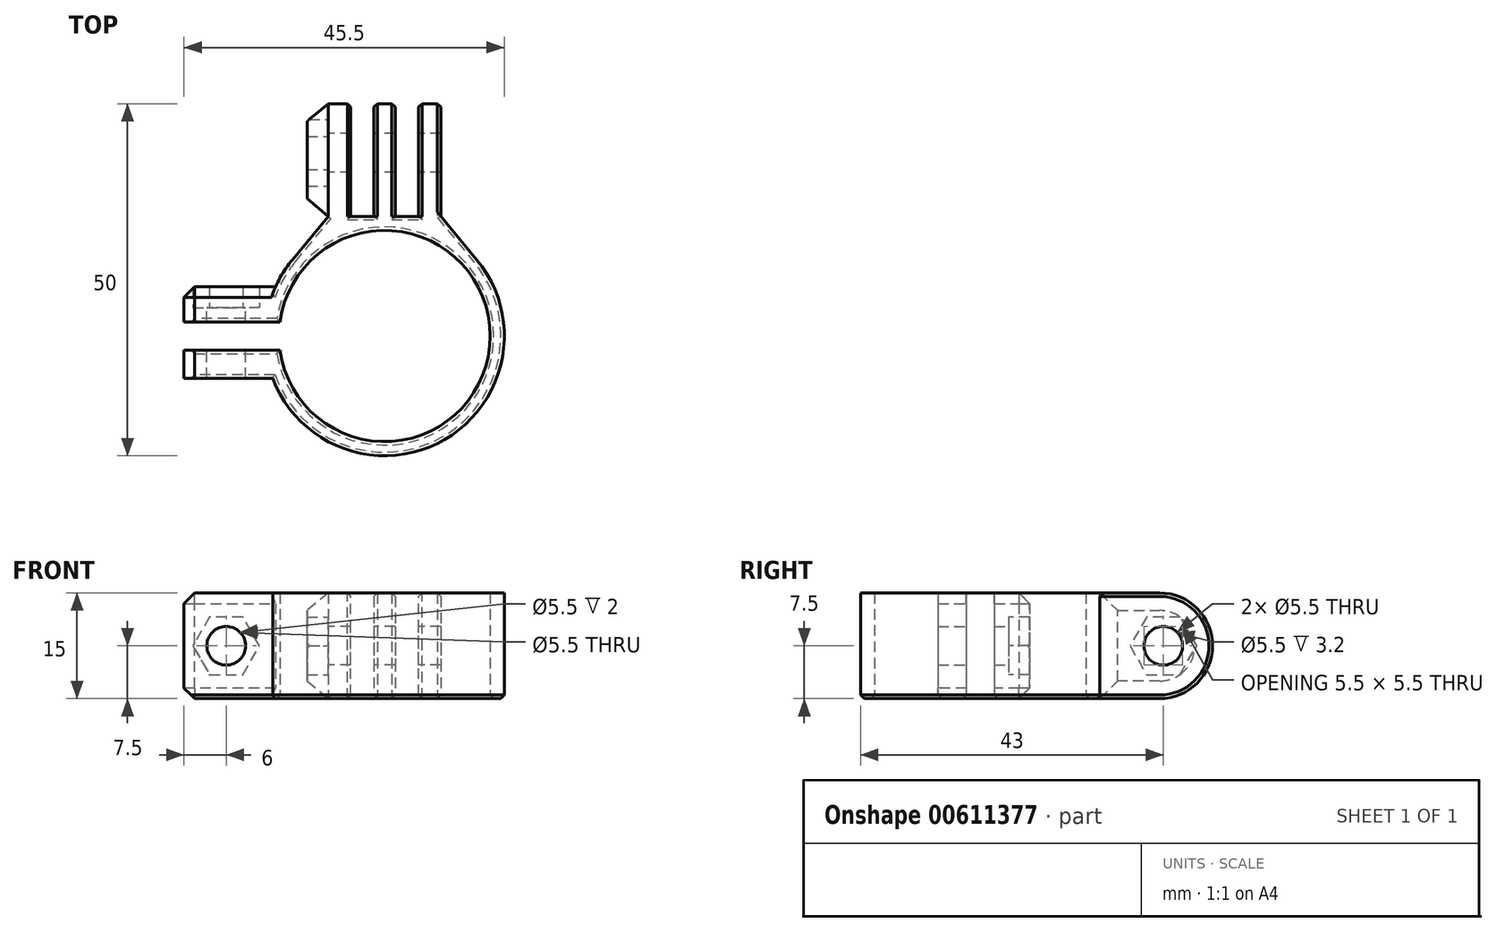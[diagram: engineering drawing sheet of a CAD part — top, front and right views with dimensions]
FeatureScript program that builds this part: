
annotation { "Feature Type Name" : "Feature", "Feature Type Description" : "" }
export const myFeature = defineFeature(function(context is Context, id is Id, definition is map)
    precondition{}
    {
        {
            var Q0;
            Q0=qCreatedBy(makeId("Top.planeOp"),FACE);
            var sketch = newSketch(context, id + "F0", { "sketchPlane" : qUnion([Q0])});
            skCircle(sketch, "E0", {"center": v(0, 0) * mm, "radius": 15 * mm});
            skCircle(sketch, "E1", {"center": v(0, 0) * mm, "radius": 17 * mm});
            skLineSegment(sketch, "E2", {"start": v(0, 17) * mm, "end": v(8, 17) * mm});
            skLineSegment(sketch, "E3", {"start": v(0, 17) * mm, "end": v(-8, 17) * mm});
            skLineSegment(sketch, "E4", {"start": v(-8, 17) * mm, "end": v(-13.1, 10.84) * mm});
            skLineSegment(sketch, "E5", {"start": v(8, 17) * mm, "end": v(13.1, 10.84) * mm});
            skLineSegment(sketch, "E6", {"start": v(13.1, 10.84) * mm, "end": v(11.56, 9.56) * mm});
            skLineSegment(sketch, "E7", {"start": v(-13.1, 10.84) * mm, "end": v(-11.56, 9.56) * mm});
            skLineSegment(sketch, "E8.bottom", {"start": v(-28.5, 2) * mm, "end": v(-10, 2) * mm});
            skLineSegment(sketch, "E8.top", {"start": v(-28.5, -2) * mm, "end": v(-10, -2) * mm});
            skLineSegment(sketch, "E8.left", {"start": v(-28.5, 2) * mm, "end": v(-28.5, -2) * mm});
            skLineSegment(sketch, "E8.right", {"start": v(-10, 2) * mm, "end": v(-10, -2) * mm});
            skLineSegment(sketch, "E9.bottom", {"start": v(-28.5, 2) * mm, "end": v(-16.52, 2) * mm});
            skLineSegment(sketch, "E9.top", {"start": v(-28.5, 4) * mm, "end": v(-16.52, 4) * mm});
            skLineSegment(sketch, "E9.left", {"start": v(-28.5, 2) * mm, "end": v(-28.5, 4) * mm});
            skLineSegment(sketch, "E9.right", {"start": v(-16.52, 2) * mm, "end": v(-16.52, 4) * mm});
            skLineSegment(sketch, "E10.bottom", {"start": v(-28.5, -2) * mm, "end": v(-16.52, -2) * mm});
            skLineSegment(sketch, "E10.top", {"start": v(-28.5, -4) * mm, "end": v(-16.52, -4) * mm});
            skLineSegment(sketch, "E10.left", {"start": v(-28.5, -2) * mm, "end": v(-28.5, -4) * mm});
            skLineSegment(sketch, "E10.right", {"start": v(-16.52, -2) * mm, "end": v(-16.52, -4) * mm});
            skSolve(sketch);
        }
        {
            var Q0;
            {var subQ0=sQuery(id+"F0.wireOp",EDGE,"E9.top");Q0=makeQuery(id+"F0.imprint","IMPRINT",FACE,{"disambiguationData":[TD([[makeQuery(id+"F0.imprint","IMPRINT",EDGE,{"derivedFrom":subQ0}),-1.0]])]});}
            var Q1;
            {var subQ0=sQuery(id+"F0.wireOp",EDGE,"E9.right");Q1=makeQuery(id+"F0.imprint","IMPRINT",FACE,{"disambiguationData":[TD([[makeQuery(id+"F0.imprint","IMPRINT",EDGE,{"derivedFrom":subQ0}),1.0]])]});}
            var Q2;
            {var subQ4=sQuery(id+"F0.wireOp",EDGE,"E7");Q2=makeQuery(id+"F0.imprint","IMPRINT",FACE,{"disambiguationData":[TD([[makeQuery(id+"F0.imprint","IMPRINT",EDGE,{"derivedFrom":subQ4}),-1.0]])]});}
            var Q3;
            {var subQ2=sQuery(id+"F0.wireOp",EDGE,"E6");Q3=makeQuery(id+"F0.imprint","IMPRINT",FACE,{"disambiguationData":[TD([[makeQuery(id+"F0.imprint","IMPRINT",EDGE,{"derivedFrom":subQ2}),-1.0]])]});}
            var Q4;
            {var subQ0=sQuery(id+"F0.wireOp",EDGE,"E3");Q4=makeQuery(id+"F0.imprint","IMPRINT",FACE,{"disambiguationData":[TD([[makeQuery(id+"F0.imprint","IMPRINT",EDGE,{"derivedFrom":subQ0}),1.0]])]});}
            var Q5;
            {var subQ0=sQuery(id+"F0.wireOp",EDGE,"E2");Q5=makeQuery(id+"F0.imprint","IMPRINT",FACE,{"disambiguationData":[TD([[makeQuery(id+"F0.imprint","IMPRINT",EDGE,{"derivedFrom":subQ0}),-1.0]])]});}
            var Q6;
            {var subQ4=sQuery(id+"F0.wireOp",EDGE,"E6");Q6=makeQuery(id+"F0.imprint","IMPRINT",FACE,{"disambiguationData":[TD([[makeQuery(id+"F0.imprint","IMPRINT",EDGE,{"derivedFrom":subQ4}),1.0]])]});}
            var Q7;
            {var subQ0=sQuery(id+"F0.wireOp",EDGE,"E10.right");Q7=makeQuery(id+"F0.imprint","IMPRINT",FACE,{"disambiguationData":[TD([[makeQuery(id+"F0.imprint","IMPRINT",EDGE,{"derivedFrom":subQ0}),-1.0]])]});}
            var Q8;
            {var subQ0=sQuery(id+"F0.wireOp",EDGE,"E10.top");Q8=makeQuery(id+"F0.imprint","IMPRINT",FACE,{"disambiguationData":[TD([[makeQuery(id+"F0.imprint","IMPRINT",EDGE,{"derivedFrom":subQ0}),1.0]])]});}
            extrude(context, id + "F1", {"entities" : qUnion([Q0, Q1, Q2, Q3, Q4, Q5, Q6, Q7, Q8]), "depth" : 15 * mm, "offsetDistance" : 25 * mm});
        }
        {
            var Q0;
            Q0=makeQuery(id+"F1.opExtrude","SWEPT_FACE",FACE,{"disambiguationData":[OSD([sQuery(id+"F0.wireOp",EDGE,"E9.top")])]});
            var sketch = newSketch(context, id + "F2", { "sketchPlane" : qUnion([Q0])});
            skCircle(sketch, "E11", {"center": v(22.5, 7.5) * mm, "radius": 2.75 * mm});
            skCircle(sketch, "E12.cCircle", {"center": v(22.5, 7.5) * mm, "radius": 4.1 * mm, "construction": true});
            skLineSegment(sketch, "E12.0", {"start": v(27.23, 7.5) * mm, "end": v(24.87, 3.4) * mm});
            skLineSegment(sketch, "E12.1", {"start": v(24.87, 3.4) * mm, "end": v(20.13, 3.4) * mm});
            skLineSegment(sketch, "E12.2", {"start": v(20.13, 3.4) * mm, "end": v(17.77, 7.5) * mm});
            skLineSegment(sketch, "E12.3", {"start": v(17.77, 7.5) * mm, "end": v(20.13, 11.6) * mm});
            skLineSegment(sketch, "E12.4", {"start": v(20.13, 11.6) * mm, "end": v(24.87, 11.6) * mm});
            skLineSegment(sketch, "E12.5", {"start": v(24.87, 11.6) * mm, "end": v(27.23, 7.5) * mm});
            skPoint(sketch, "E12.0.midPoint", {"position": v(26.05, 5.45) * mm});
            skLineSegment(sketch, "E13.0", {"start": v(16.03, 7.5) * mm, "end": v(19.27, 13.1) * mm});
            skLineSegment(sketch, "E13.1", {"start": v(25.73, 13.1) * mm, "end": v(28.97, 7.5) * mm});
            skLineSegment(sketch, "E13.2", {"start": v(28.97, 7.5) * mm, "end": v(25.73, 1.9) * mm});
            skLineSegment(sketch, "E13.3", {"start": v(19.27, 13.1) * mm, "end": v(25.73, 13.1) * mm});
            skLineSegment(sketch, "E13.4", {"start": v(25.73, 1.9) * mm, "end": v(19.27, 1.9) * mm});
            skLineSegment(sketch, "E13.5", {"start": v(19.27, 1.9) * mm, "end": v(16.03, 7.5) * mm});
            skSolve(sketch);
        }
        {
            var Q0;
            Q0=makeQuery(id+"F2.imprint","IMPRINT",FACE,{"disambiguationData":[TD([[makeQuery(id+"F2.imprint","IMPRINT",EDGE,{"derivedFrom":sQuery(id+"F2.wireOp",EDGE,"E11")}),1.0]])]});
            extrude(context, id + "F3", {"entities" : qUnion([Q0]), "operationType" : NewBodyOperationType.REMOVE, "endBound" : BoundingType.THROUGH_ALL, "oppositeDirection" : true, "depth" : 25 * mm, "offsetDistance" : 25 * mm});
        }
        {
            var Q0;
            Q0=makeQuery(id+"F2.imprint","IMPRINT",FACE,{"disambiguationData":[TD([[makeQuery(id+"F2.imprint","IMPRINT",EDGE,{"derivedFrom":sQuery(id+"F2.wireOp",EDGE,"E13.0")}),1.0]])]});
            var Q1;
            Q1=makeQuery(id+"F2.imprint","IMPRINT",FACE,{"disambiguationData":[TD([[makeQuery(id+"F2.imprint","IMPRINT",EDGE,{"derivedFrom":sQuery(id+"F2.wireOp",EDGE,"E12.0")}),1.0]])]});
            var Q2;
            {var subQ1=sQuery(id+"F2.wireOp",EDGE,"E13.4");Q2=makeQuery(id+"F2.imprint","IMPRINT",FACE,{"disambiguationData":[TD([[makeQuery(id+"F2.imprint","IMPRINT",EDGE,{"derivedFrom":subQ1}),1.0]])]});}
            extrude(context, id + "F4", {"entities" : qUnion([Q0, Q1, Q2]), "operationType" : NewBodyOperationType.ADD, "depth" : 3 * mm, "offsetDistance" : 25 * mm});
        }
        {
            var Q0;
            Q0=makeQuery(id+"F4.opExtrude","SWEPT_FACE",FACE,{"disambiguationData":[OSD([sQuery(id+"F0.wireOp",EDGE,"E1"),sQuery(id+"F0.wireOp",EDGE,"E9.top"),sQuery(id+"F0.wireOp",EDGE,"E9.right")])]});
            extrude(context, id + "F5", {"entities" : qUnion([Q0]), "operationType" : NewBodyOperationType.ADD, "endBound" : BoundingType.UP_TO_NEXT, "depth" : 25 * mm, "offsetDistance" : 25 * mm});
        }
        {
            var Q0;
            Q0=makeQuery(id+"F1.opExtrude","SWEPT_FACE",FACE,{"disambiguationData":[OSD([sQuery(id+"F0.wireOp",EDGE,"E2"),sQuery(id+"F0.wireOp",EDGE,"E3")])]});
            var sketch = newSketch(context, id + "F6", { "sketchPlane" : qUnion([Q0])});
            skLineSegment(sketch, "E14.bottom", {"start": v(-8, 0) * mm, "end": v(-4.8, 0) * mm});
            skLineSegment(sketch, "E14.top", {"start": v(-8, 15) * mm, "end": v(-4.8, 15) * mm});
            skLineSegment(sketch, "E14.left", {"start": v(-8, 0) * mm, "end": v(-8, 15) * mm});
            skLineSegment(sketch, "E14.right", {"start": v(-4.8, 0) * mm, "end": v(-4.8, 15) * mm});
            skLineSegment(sketch, "E15.bottom", {"start": v(8, 0) * mm, "end": v(4.8, 0) * mm});
            skLineSegment(sketch, "E15.top", {"start": v(8, 15) * mm, "end": v(4.8, 15) * mm});
            skLineSegment(sketch, "E15.left", {"start": v(8, 0) * mm, "end": v(8, 15) * mm});
            skLineSegment(sketch, "E15.right", {"start": v(4.8, 0) * mm, "end": v(4.8, 15) * mm});
            skLineSegment(sketch, "E16.bottom", {"start": v(-1.5, 15) * mm, "end": v(1.5, 15) * mm});
            skLineSegment(sketch, "E16.top", {"start": v(-1.5, 0) * mm, "end": v(1.5, 0) * mm});
            skLineSegment(sketch, "E16.left", {"start": v(-1.5, 15) * mm, "end": v(-1.5, 0) * mm});
            skLineSegment(sketch, "E16.right", {"start": v(1.5, 15) * mm, "end": v(1.5, 0) * mm});
            skSolve(sketch);
        }
        {
            var Q0;
            Q0=makeQuery(id+"F6.imprint","IMPRINT",FACE,{"disambiguationData":[TD([[makeQuery(id+"F6.imprint","IMPRINT",EDGE,{"derivedFrom":sQuery(id+"F6.wireOp",EDGE,"E14.bottom")}),1.0]])]});
            var Q1;
            Q1=makeQuery(id+"F6.imprint","IMPRINT",FACE,{"disambiguationData":[TD([[makeQuery(id+"F6.imprint","IMPRINT",EDGE,{"derivedFrom":sQuery(id+"F6.wireOp",EDGE,"E16.bottom")}),-1.0]])]});
            var Q2;
            Q2=makeQuery(id+"F6.imprint","IMPRINT",FACE,{"disambiguationData":[TD([[makeQuery(id+"F6.imprint","IMPRINT",EDGE,{"derivedFrom":sQuery(id+"F6.wireOp",EDGE,"E15.bottom")}),1.0]])]});
            extrude(context, id + "F7", {"entities" : qUnion([Q0, Q1, Q2]), "operationType" : NewBodyOperationType.ADD, "depth" : 16 * mm, "offsetDistance" : 25 * mm});
        }
        {
            var Q0;
            Q0=makeQuery(id+"F7.opExtrude","SWEPT_FACE",FACE,{"disambiguationData":[OSD([sQuery(id+"F6.wireOp",EDGE,"E15.left")])]});
            var sketch = newSketch(context, id + "F8", { "sketchPlane" : qUnion([Q0])});
            skCircle(sketch, "E17", {"center": v(-26, 7.5) * mm, "radius": 2.75 * mm});
            skPoint(sketch, "E18.0.midPoint", {"position": v(-30.1, 7.5) * mm});
            skCircle(sketch, "E19.cCircle", {"center": v(-26, 7.5) * mm, "radius": 4.1 * mm, "construction": true});
            skLineSegment(sketch, "E19.0", {"start": v(-28.37, 11.6) * mm, "end": v(-23.63, 11.6) * mm});
            skLineSegment(sketch, "E19.1", {"start": v(-23.63, 11.6) * mm, "end": v(-21.27, 7.5) * mm});
            skLineSegment(sketch, "E19.2", {"start": v(-21.27, 7.5) * mm, "end": v(-23.63, 3.4) * mm});
            skLineSegment(sketch, "E19.3", {"start": v(-23.63, 3.4) * mm, "end": v(-28.37, 3.4) * mm});
            skLineSegment(sketch, "E19.4", {"start": v(-28.37, 3.4) * mm, "end": v(-30.73, 7.5) * mm});
            skLineSegment(sketch, "E19.5", {"start": v(-30.73, 7.5) * mm, "end": v(-28.37, 11.6) * mm});
            skPoint(sketch, "E19.0.midPoint", {"position": v(-26, 11.6) * mm});
            skLineSegment(sketch, "E20.0", {"start": v(-22.77, 13.1) * mm, "end": v(-19.53, 7.5) * mm});
            skLineSegment(sketch, "E20.1", {"start": v(-22.77, 1.9) * mm, "end": v(-29.23, 1.9) * mm});
            skLineSegment(sketch, "E20.2", {"start": v(-29.23, 1.9) * mm, "end": v(-32.47, 7.5) * mm});
            skLineSegment(sketch, "E20.3", {"start": v(-19.53, 7.5) * mm, "end": v(-22.77, 1.9) * mm});
            skLineSegment(sketch, "E20.4", {"start": v(-32.47, 7.5) * mm, "end": v(-29.23, 13.1) * mm});
            skLineSegment(sketch, "E20.5", {"start": v(-29.23, 13.1) * mm, "end": v(-22.77, 13.1) * mm});
            skSolve(sketch);
        }
        {
            var Q0;
            Q0=makeQuery(id+"F8.imprint","IMPRINT",FACE,{"disambiguationData":[TD([[makeQuery(id+"F8.imprint","IMPRINT",EDGE,{"derivedFrom":sQuery(id+"F8.wireOp",EDGE,"E17")}),1.0]])]});
            extrude(context, id + "F9", {"entities" : qUnion([Q0]), "operationType" : NewBodyOperationType.REMOVE, "endBound" : BoundingType.THROUGH_ALL, "oppositeDirection" : true, "depth" : 25 * mm, "offsetDistance" : 25 * mm});
        }
        {
            var Q0;
            Q0=makeQuery(id+"F8.imprint","IMPRINT",FACE,{"disambiguationData":[TD([[makeQuery(id+"F8.imprint","IMPRINT",EDGE,{"derivedFrom":sQuery(id+"F8.wireOp",EDGE,"E19.0")}),1.0]])]});
            extrude(context, id + "F10", {"entities" : qUnion([Q0]), "operationType" : NewBodyOperationType.ADD, "depth" : 3 * mm, "offsetDistance" : 25 * mm});
        }
        {
            var Q0;
            Q0=makeQuery(id+"F7.opExtrude","CAP_EDGE",EDGE,{"disambiguationData":[OSD([sQuery(id+"F6.wireOp",EDGE,"E14.bottom")])],"isStart":false});
            var Q1;
            Q1=makeQuery(id+"F7.opExtrude","CAP_EDGE",EDGE,{"disambiguationData":[OSD([sQuery(id+"F6.wireOp",EDGE,"E16.top")])],"isStart":false});
            var Q2;
            Q2=makeQuery(id+"F7.opExtrude","CAP_EDGE",EDGE,{"disambiguationData":[OSD([sQuery(id+"F6.wireOp",EDGE,"E15.bottom")])],"isStart":false});
            var Q3;
            Q3=makeQuery(id+"F7.opExtrude","CAP_EDGE",EDGE,{"disambiguationData":[OSD([sQuery(id+"F6.wireOp",EDGE,"E15.top")])],"isStart":false});
            var Q4;
            Q4=makeQuery(id+"F7.opExtrude","CAP_EDGE",EDGE,{"disambiguationData":[OSD([sQuery(id+"F6.wireOp",EDGE,"E16.bottom")])],"isStart":false});
            var Q5;
            Q5=makeQuery(id+"F7.opExtrude","CAP_EDGE",EDGE,{"disambiguationData":[OSD([sQuery(id+"F6.wireOp",EDGE,"E14.top")])],"isStart":false});
            fillet(context, id + "F11", {"entities" : qUnion([Q0, Q1, Q2, Q3, Q4, Q5]), "radius" : 7.5 * mm, "tangentPropagation" : true, "allowEdgeOverflow" : false});
        }
        {
            var Q0;
            {var subQ7=sQuery(id+"F0.wireOp",EDGE,"E4");var subQ19=sQuery(id+"F6.wireOp",EDGE,"E15.left");Q0=makeQuery(id+"F10.boolean.opBoolean","SPLIT",FACE,{"disambiguationData":[TD([makeQuery(id+"F1.opExtrude","SWEPT_FACE",FACE,{"disambiguationData":[OSD([subQ7])]})])],"derivedFrom":makeQuery(id+"F7.opExtrude","SWEPT_FACE",FACE,{"disambiguationData":[OSD([subQ19])]})});}
            extrude(context, id + "F12", {"entities" : qUnion([Q0]), "operationType" : NewBodyOperationType.ADD, "depth" : 3 * mm, "offsetDistance" : 25 * mm});
        }
        {
            var Q0;
            Q0=makeQuery(id+"F12.opExtrude","CAP_EDGE",EDGE,{"disambiguationData":[OSD([sQuery(id+"F0.wireOp",EDGE,"E3"),sQuery(id+"F0.wireOp",EDGE,"E4"),sQuery(id+"F6.wireOp",EDGE,"E15.left")])],"isStart":false});
            var Q1;
            {var subQ7=sQuery(id+"F0.wireOp",EDGE,"E4");var subQ19=sQuery(id+"F6.wireOp",EDGE,"E15.left");var subQ20=sQuery(id+"F6.wireOp",EDGE,"E15.top");Q1=makeQuery(id+"F12.opExtrude","CAP_EDGE",EDGE,{"disambiguationData":[OSD([subQ20,subQ19]),TDD([makeQuery(id+"F11.opFillet","BLEND_EDGE",EDGE,{"blendedFrom":[makeQuery(id+"F7.opExtrude","CAP_EDGE",EDGE,{"disambiguationData":[OSD([subQ20])],"isStart":false}),makeQuery(id+"F10.boolean.opBoolean","SPLIT",FACE,{"disambiguationData":[TD([makeQuery(id+"F1.opExtrude","SWEPT_FACE",FACE,{"disambiguationData":[OSD([subQ7])]})])],"derivedFrom":makeQuery(id+"F7.opExtrude","SWEPT_FACE",FACE,{"disambiguationData":[OSD([subQ19])]})})],"blendedInto":[makeQuery(id+"F10.boolean.opBoolean","SPLIT",FACE,{"disambiguationData":[TD([makeQuery(id+"F1.opExtrude","SWEPT_FACE",FACE,{"disambiguationData":[OSD([subQ7])]})])],"derivedFrom":makeQuery(id+"F7.opExtrude","SWEPT_FACE",FACE,{"disambiguationData":[OSD([subQ19])]})})]})])],"isStart":false});}
            chamfer(context, id + "F13", {"entities" : qUnion([Q0, Q1]), "chamferType" : ChamferType.TWO_OFFSETS, "width1" : 3 * mm, "oppositeDirection" : false, "width2" : 2.5 * mm, "tangentPropagation" : true});
        }
        {
            var Q0;
            {var subQ0=sQuery(id+"F0.wireOp",EDGE,"E9.top");var subQ1=makeQuery(id+"F1.opExtrude","CAP_EDGE",EDGE,{"disambiguationData":[OSD([subQ0])],"isStart":true});var subQ2=sQuery(id+"F0.wireOp",EDGE,"E9.right");var subQ3=sQuery(id+"F0.wireOp",EDGE,"E1");Q0=makeQuery(id+"F5.boolean.opBoolean","MERGE",EDGE,{"derivedFrom":[makeQuery(id+"F4.opExtrude","CAP_EDGE",EDGE,{"disambiguationData":[OSD([subQ0]),TDD([makeQuery(id+"F2.imprint","IMPRINT",EDGE,{"derivedFrom":subQ1})])],"isStart":false}),makeQuery(id+"F5.opExtrude","SWEPT_EDGE",EDGE,{"disambiguationData":[OSD([subQ3,subQ0,subQ2]),TDD([makeQuery(id+"F4.opExtrude","CAP_VERTEX",VERTEX,{"disambiguationData":[OSD([subQ3,subQ0,subQ2]),TDD([makeQuery(id+"F2.imprint","INTERSECT",VERTEX,{"derivedFrom":[makeQuery(id+"F1.opExtrude","SWEPT_EDGE",EDGE,{"disambiguationData":[OSD([subQ3,subQ0,subQ2])]}),subQ1]})])],"isStart":false})])]})]});}
            var Q1;
            Q1=makeQuery(id+"F4.opExtrude","CAP_EDGE",EDGE,{"disambiguationData":[OSD([sQuery(id+"F0.wireOp",EDGE,"E9.top"),sQuery(id+"F0.wireOp",EDGE,"E9.left")])],"isStart":false});
            var Q2;
            {var subQ0=sQuery(id+"F0.wireOp",EDGE,"E9.top");var subQ1=makeQuery(id+"F1.opExtrude","CAP_EDGE",EDGE,{"disambiguationData":[OSD([subQ0])],"isStart":false});var subQ2=sQuery(id+"F0.wireOp",EDGE,"E9.right");var subQ3=sQuery(id+"F0.wireOp",EDGE,"E1");Q2=makeQuery(id+"F5.boolean.opBoolean","MERGE",EDGE,{"derivedFrom":[makeQuery(id+"F4.opExtrude","CAP_EDGE",EDGE,{"disambiguationData":[OSD([subQ0]),TDD([makeQuery(id+"F2.imprint","IMPRINT",EDGE,{"derivedFrom":subQ1})])],"isStart":false}),makeQuery(id+"F5.opExtrude","SWEPT_EDGE",EDGE,{"disambiguationData":[OSD([subQ3,subQ0,subQ2]),TDD([makeQuery(id+"F4.opExtrude","CAP_VERTEX",VERTEX,{"disambiguationData":[OSD([subQ3,subQ0,subQ2]),TDD([makeQuery(id+"F2.imprint","INTERSECT",VERTEX,{"derivedFrom":[makeQuery(id+"F1.opExtrude","SWEPT_EDGE",EDGE,{"disambiguationData":[OSD([subQ3,subQ0,subQ2])]}),subQ1]})])],"isStart":false})])]})]});}
            var Q3;
            {var subQ0=sQuery(id+"F0.wireOp",EDGE,"E9.top");var subQ1=sQuery(id+"F0.wireOp",EDGE,"E9.left");Q3=makeQuery(id+"F4.boolean.opBoolean","MERGE",EDGE,{"derivedFrom":[makeQuery(id+"F1.opExtrude","CAP_EDGE",EDGE,{"disambiguationData":[OSD([subQ1])],"isStart":false}),makeQuery(id+"F4.opExtrude","SWEPT_EDGE",EDGE,{"disambiguationData":[OSD([subQ0,subQ1]),TDD([makeQuery(id+"F2.imprint","INTERSECT",VERTEX,{"derivedFrom":[makeQuery(id+"F1.opExtrude","SWEPT_EDGE",EDGE,{"disambiguationData":[OSD([subQ0,subQ1])]}),makeQuery(id+"F1.opExtrude","CAP_EDGE",EDGE,{"disambiguationData":[OSD([subQ0])],"isStart":false})]})])]})]});}
            var Q4;
            {var subQ0=sQuery(id+"F0.wireOp",EDGE,"E9.top");var subQ1=sQuery(id+"F0.wireOp",EDGE,"E9.left");Q4=makeQuery(id+"F4.boolean.opBoolean","MERGE",EDGE,{"derivedFrom":[makeQuery(id+"F1.opExtrude","CAP_EDGE",EDGE,{"disambiguationData":[OSD([subQ1])],"isStart":true}),makeQuery(id+"F4.opExtrude","SWEPT_EDGE",EDGE,{"disambiguationData":[OSD([subQ0,subQ1]),TDD([makeQuery(id+"F2.imprint","INTERSECT",VERTEX,{"derivedFrom":[makeQuery(id+"F1.opExtrude","SWEPT_EDGE",EDGE,{"disambiguationData":[OSD([subQ0,subQ1])]}),makeQuery(id+"F1.opExtrude","CAP_EDGE",EDGE,{"disambiguationData":[OSD([subQ0])],"isStart":true})]})])]})]});}
            var Q5;
            Q5=makeQuery(id+"F1.opExtrude","CAP_EDGE",EDGE,{"disambiguationData":[OSD([sQuery(id+"F0.wireOp",EDGE,"E10.left")])],"isStart":true});
            var Q6;
            Q6=makeQuery(id+"F1.opExtrude","CAP_EDGE",EDGE,{"disambiguationData":[OSD([sQuery(id+"F0.wireOp",EDGE,"E10.left")])],"isStart":false});
            chamfer(context, id + "F14", {"entities" : qUnion([Q0, Q1, Q2, Q3, Q4, Q5, Q6]), "width" : 1.5 * mm, "tangentPropagation" : true});
        }
        {
            var Q0;
            Q0=makeQuery(id+"F1.opExtrude","SWEPT_FACE",FACE,{"disambiguationData":[OSD([sQuery(id+"F0.wireOp",EDGE,"E10.top")])]});
            extrude(context, id + "F15", {"entities" : qUnion([Q0]), "operationType" : NewBodyOperationType.ADD, "depth" : 2 * mm, "offsetDistance" : 25 * mm});
        }
        {
            var Q0;
            Q0=makeQuery(id+"F15.opExtrude","SWEPT_FACE",FACE,{"disambiguationData":[OSD([sQuery(id+"F0.wireOp",EDGE,"E1"),sQuery(id+"F0.wireOp",EDGE,"E10.top"),sQuery(id+"F0.wireOp",EDGE,"E10.right")])]});
            extrude(context, id + "F16", {"entities" : qUnion([Q0]), "operationType" : NewBodyOperationType.ADD, "endBound" : BoundingType.UP_TO_NEXT, "depth" : 25 * mm, "offsetDistance" : 25 * mm});
        }
        {
            var Q0;
            Q0=makeQuery(id+"F1.opExtrude","CAP_EDGE",EDGE,{"disambiguationData":[OSD([sQuery(id+"F0.wireOp",EDGE,"E0")])],"isStart":true});
            var Q1;
            Q1=makeQuery(id+"F1.opExtrude","CAP_EDGE",EDGE,{"disambiguationData":[OSD([sQuery(id+"F0.wireOp",EDGE,"E8.bottom"),sQuery(id+"F0.wireOp",EDGE,"E9.bottom")])],"isStart":true});
            var Q2;
            Q2=makeQuery(id+"F1.opExtrude","CAP_EDGE",EDGE,{"disambiguationData":[OSD([sQuery(id+"F0.wireOp",EDGE,"E8.top"),sQuery(id+"F0.wireOp",EDGE,"E10.bottom")])],"isStart":true});
            var Q3;
            {var subQ0=sQuery(id+"F0.wireOp",EDGE,"E1");Q3=makeQuery(id+"F1.opExtrude","CAP_EDGE",EDGE,{"disambiguationData":[OSD([subQ0]),TDD([makeQuery(id+"F0.imprint","IMPRINT",EDGE,{"disambiguationData":[TD([[makeQuery(id+"F0.imprint","INTERSECT",VERTEX,{"derivedFrom":[subQ0,sQuery(id+"F0.wireOp",EDGE,"E5"),sQuery(id+"F0.wireOp",EDGE,"E6")]}),1.0]])],"derivedFrom":subQ0})])],"isStart":true});}
            var Q4;
            Q4=makeQuery(id+"F1.opExtrude","CAP_EDGE",EDGE,{"disambiguationData":[OSD([sQuery(id+"F0.wireOp",EDGE,"E4")])],"isStart":true});
            var Q5;
            Q5=makeQuery(id+"F7.opExtrude","SWEPT_EDGE",EDGE,{"disambiguationData":[OSD([sQuery(id+"F0.wireOp",EDGE,"E2"),sQuery(id+"F0.wireOp",EDGE,"E3"),sQuery(id+"F6.wireOp",EDGE,"E15.bottom"),sQuery(id+"F6.wireOp",EDGE,"E15.right")])]});
            var Q6;
            {var subQ4=sQuery(id+"F0.wireOp",EDGE,"E3");var subQ5=sQuery(id+"F0.wireOp",EDGE,"E2");Q6=makeQuery(id+"F7.boolean.opBoolean","SPLIT",EDGE,{"disambiguationData":[TD([makeQuery(id+"F7.opExtrude","SWEPT_FACE",FACE,{"disambiguationData":[OSD([sQuery(id+"F6.wireOp",EDGE,"E15.right")])]})])],"derivedFrom":makeQuery(id+"F1.opExtrude","CAP_EDGE",EDGE,{"disambiguationData":[OSD([subQ5,subQ4])],"isStart":true})});}
            var Q7;
            Q7=makeQuery(id+"F7.opExtrude","SWEPT_EDGE",EDGE,{"disambiguationData":[OSD([sQuery(id+"F0.wireOp",EDGE,"E2"),sQuery(id+"F0.wireOp",EDGE,"E3"),sQuery(id+"F6.wireOp",EDGE,"E16.top"),sQuery(id+"F6.wireOp",EDGE,"E16.right")])]});
            var Q8;
            Q8=makeQuery(id+"F7.opExtrude","SWEPT_EDGE",EDGE,{"disambiguationData":[OSD([sQuery(id+"F0.wireOp",EDGE,"E2"),sQuery(id+"F0.wireOp",EDGE,"E3"),sQuery(id+"F6.wireOp",EDGE,"E16.top"),sQuery(id+"F6.wireOp",EDGE,"E16.left")])]});
            var Q9;
            {var subQ4=sQuery(id+"F0.wireOp",EDGE,"E3");var subQ5=sQuery(id+"F0.wireOp",EDGE,"E2");Q9=makeQuery(id+"F7.boolean.opBoolean","SPLIT",EDGE,{"disambiguationData":[TD([makeQuery(id+"F7.opExtrude","SWEPT_FACE",FACE,{"disambiguationData":[OSD([sQuery(id+"F6.wireOp",EDGE,"E14.right")])]})])],"derivedFrom":makeQuery(id+"F1.opExtrude","CAP_EDGE",EDGE,{"disambiguationData":[OSD([subQ5,subQ4])],"isStart":true})});}
            var Q10;
            Q10=makeQuery(id+"F7.opExtrude","SWEPT_EDGE",EDGE,{"disambiguationData":[OSD([sQuery(id+"F0.wireOp",EDGE,"E2"),sQuery(id+"F0.wireOp",EDGE,"E3"),sQuery(id+"F6.wireOp",EDGE,"E14.bottom"),sQuery(id+"F6.wireOp",EDGE,"E14.right")])]});
            var Q11;
            Q11=makeQuery(id+"F7.opExtrude","SWEPT_EDGE",EDGE,{"disambiguationData":[OSD([sQuery(id+"F6.wireOp",EDGE,"E14.bottom"),sQuery(id+"F6.wireOp",EDGE,"E14.left")])]});
            var Q12;
            Q12=makeQuery(id+"F1.opExtrude","CAP_EDGE",EDGE,{"disambiguationData":[OSD([sQuery(id+"F0.wireOp",EDGE,"E10.top")])],"isStart":true});
            var Q13;
            {var subQ0=sQuery(id+"F0.wireOp",EDGE,"E9.top");var subQ1=sQuery(id+"F0.wireOp",EDGE,"E9.left");Q13=makeQuery(id+"F4.boolean.opBoolean","MERGE",EDGE,{"derivedFrom":[makeQuery(id+"F1.opExtrude","CAP_EDGE",EDGE,{"disambiguationData":[OSD([subQ1])],"isStart":true}),makeQuery(id+"F4.opExtrude","SWEPT_EDGE",EDGE,{"disambiguationData":[OSD([subQ0,subQ1]),TDD([makeQuery(id+"F2.imprint","INTERSECT",VERTEX,{"derivedFrom":[makeQuery(id+"F1.opExtrude","SWEPT_EDGE",EDGE,{"disambiguationData":[OSD([subQ0,subQ1])]}),makeQuery(id+"F1.opExtrude","CAP_EDGE",EDGE,{"disambiguationData":[OSD([subQ0])],"isStart":true})]})])]})]});}
            var Q14;
            Q14=makeQuery(id+"F1.opExtrude","CAP_EDGE",EDGE,{"disambiguationData":[OSD([sQuery(id+"F0.wireOp",EDGE,"E10.left")])],"isStart":true});
            var Q15;
            {var subQ0=sQuery(id+"F0.wireOp",EDGE,"E10.right");var subQ1=sQuery(id+"F0.wireOp",EDGE,"E10.top");var subQ2=sQuery(id+"F0.wireOp",EDGE,"E1");Q15=makeQuery(id+"F16.boolean.opBoolean","MERGE",EDGE,{"derivedFrom":[makeQuery(id+"F15.opExtrude","CAP_EDGE",EDGE,{"disambiguationData":[OSD([subQ1]),TDD([makeQuery(id+"F1.opExtrude","CAP_EDGE",EDGE,{"disambiguationData":[OSD([subQ1])],"isStart":true})])],"isStart":false}),makeQuery(id+"F16.opExtrude","SWEPT_EDGE",EDGE,{"disambiguationData":[OSD([subQ2,subQ1,subQ0]),TDD([makeQuery(id+"F15.opExtrude","CAP_VERTEX",VERTEX,{"disambiguationData":[OSD([subQ2,subQ1,subQ0]),TDD([makeQuery(id+"F1.opExtrude","CAP_VERTEX",VERTEX,{"disambiguationData":[OSD([subQ2,subQ1,subQ0])],"isStart":true})])],"isStart":false})])]})]});}
            chamfer(context, id + "F17", {"entities" : qUnion([Q0, Q1, Q2, Q3, Q4, Q5, Q6, Q7, Q8, Q9, Q10, Q11, Q12, Q13, Q14, Q15]), "width" : .5 * mm, "tangentPropagation" : true});
        }
    });
